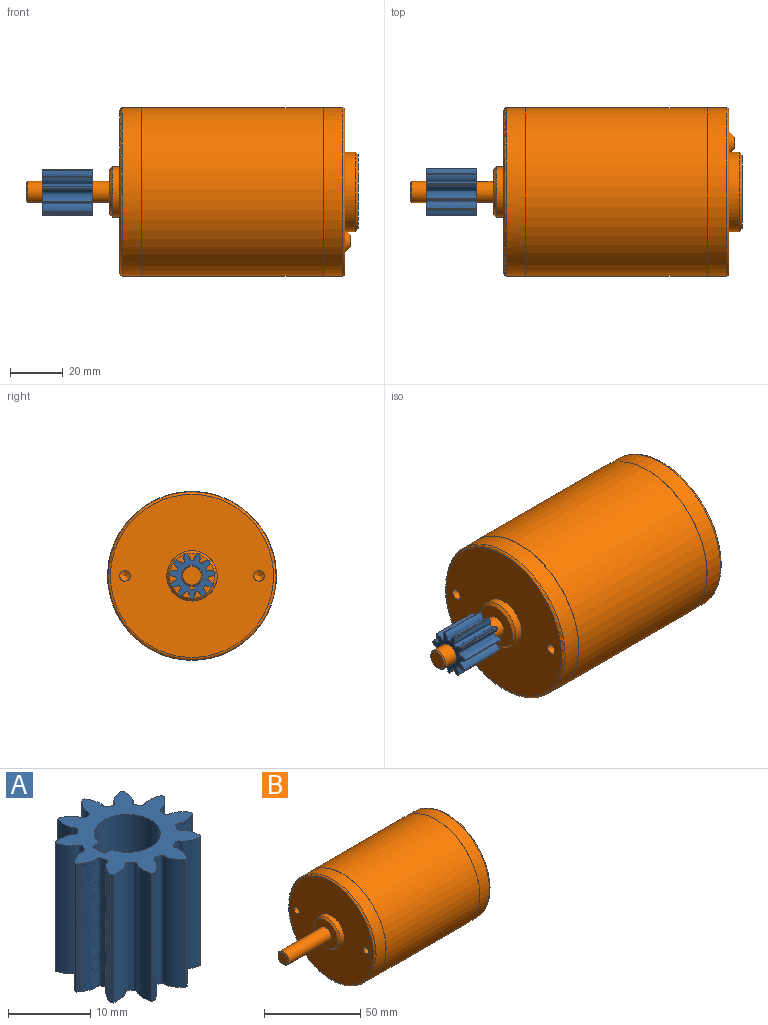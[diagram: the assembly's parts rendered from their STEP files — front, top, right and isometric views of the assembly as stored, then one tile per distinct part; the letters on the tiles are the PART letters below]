
ASSEMBLY  parts=2 mates=1
PART A: 34 faces, bbox 17.6x17.7x19.1 mm
  f0: cylinder r=4mm len=19.05mm, axis (0,0,1), area 439.9mm2, adj f17,f19,f31,f32
  f1: bspline ~9.53x0.35mm, area 4.2mm2, adj f6,f11,f17,f25
  f2: bspline ~9.53x0.41mm, area 4.2mm2, adj f3,f16,f17,f21
  f3: bspline ~9.53x0.41mm, area 4.2mm2, adj f2,f16,f19,f21
  f4: bspline ~19.05x0.44mm, area 8.3mm2, adj f15,f17,f19,f21
  f5: bspline ~19.05x0.41mm, area 8.3mm2, adj f12,f17,f19,f25
  f6: bspline ~9.53x0.35mm, area 4.2mm2, adj f1,f11,f19,f25
  f7: cylinder r=8.94mm len=19.05mm, axis (0,0,1), area 7.5mm2, adj f17,f19,f29,f30
  f8: cylinder r=8.94mm len=19.05mm, axis (0,0,1), area 7.5mm2, adj f17,f19,f28,f29
  f9: cylinder r=8.94mm len=19.05mm, axis (0,0,1), area 7.5mm2, adj f17,f19,f27,f28
  f10: cylinder r=8.94mm len=19.05mm, axis (0,0,1), area 7.5mm2, adj f17,f19,f26,f27
  f11: cylinder r=8.94mm len=19.05mm, axis (0,0,1), area 7.5mm2, adj f1,f6,f17,f19,f26
  f12: cylinder r=8.94mm len=19.05mm, axis (0,0,1), area 7.5mm2, adj f5,f17,f19,f24
  f13: cylinder r=8.94mm len=19.05mm, axis (0,0,1), area 7.5mm2, adj f17,f19,f23,f24
  f14: cylinder r=8.94mm len=19.05mm, axis (0,0,1), area 7.5mm2, adj f17,f19,f22,f23
  f15: cylinder r=8.94mm len=19.05mm, axis (0,0,1), area 7.5mm2, adj f4,f17,f19,f22
  f16: cylinder r=8.94mm len=19.05mm, axis (0,0,1), area 7.5mm2, adj f2,f3,f17,f19,f20
  f17: plane 17.74x17.57mm, normal (0,0,1), area 121.8mm2, adj f0,f1,f2,f4,f5,f7,f8,f9
  f18: cylinder r=8.94mm len=19.05mm, axis (0,0,1), area 7.5mm2, adj f17,f19,f20,f30
  f19: plane 17.74x17.57mm, normal (0,0,-1), area 121.8mm2, adj f0,f3,f4,f5,f6,f7,f8,f9
  f20: bspline ~19.05x4.65mm, area 140.4mm2, adj f16,f17,f18,f19
  f21: bspline ~19.05x3.33mm, area 123.7mm2, adj f2,f3,f4,f17,f19
  f22: bspline ~19.05x4.23mm, area 140.4mm2, adj f14,f15,f17,f19
  f23: bspline ~19.05x4.61mm, area 140.4mm2, adj f13,f14,f17,f19
  f24: bspline ~19.05x3.78mm, area 140.4mm2, adj f12,f13,f17,f19
  f25: bspline ~19.05x3.79mm, area 123.7mm2, adj f1,f5,f6,f17,f19
  f26: bspline ~19.05x4.47mm, area 140.4mm2, adj f10,f11,f17,f19
  f27: bspline ~19.05x3.78mm, area 140.4mm2, adj f9,f10,f17,f19
  f28: bspline ~19.05x4.61mm, area 140.4mm2, adj f8,f9,f17,f19
  f29: bspline ~19.05x4.23mm, area 140.4mm2, adj f7,f8,f17,f19
  f30: bspline ~19.05x3.92mm, area 140.4mm2, adj f7,f17,f18,f19
  f31: plane 19.05x1.13mm, normal (0,-1,0), area 21.5mm2, adj f0,f17,f19,f33
  f32: plane 19.05x1.13mm, normal (0,1,0), area 21.5mm2, adj f0,f17,f19,f33
  f33: plane 19.05x2.02mm, normal (1,0,0), area 38.5mm2, adj f17,f19,f31,f32
PART B: 33 faces, bbox 125.8x69x69 mm
  f0: cone r=4mm half-angle=45deg, axis (1,0,0), area 16.7mm2, adj f18,f22
  f1: cone r=9.53mm half-angle=45deg, axis (1,0,0), area 81.4mm2, adj f13,f27
  f2: cone r=14.02mm half-angle=45deg, axis (-1,0,0), area 131.2mm2, adj f17,f23
  f3: cone r=2.12mm half-angle=45deg, axis (-1,0,0), area 62.9mm2, adj f5,f29
  f4: cone r=2.12mm half-angle=45deg, axis (-1,0,0), area 62.9mm2, adj f6,f28
  f5: cylinder r=4.32mm len=8.64mm, axis (-1,0,0), area 1.3mm2, adj f3,f21
  f6: cylinder r=4.32mm len=8.64mm, axis (-1,0,0), area 1.3mm2, adj f4,f21
  f7: cone r=2.02mm half-angle=59deg, axis (-1,0,0), area 14.9mm2, adj f8
  f8: cylinder r=2.02mm len=13.61mm, axis (-1,0,0), area 172.7mm2, adj f7,f26
  f9: cone r=2.02mm half-angle=59deg, axis (-1,0,0), area 14.9mm2, adj f10
  f10: cylinder r=2.02mm len=13.61mm, axis (-1,0,0), area 172.7mm2, adj f9,f26
  f11: torus R=30.88mm, axis (1,0,0), area 311mm2, adj f16,f21
  f12: torus R=30.88mm, axis (-1,0,0), area 311mm2, adj f14,f26
  f13: cylinder r=9.53mm len=19.05mm, axis (1,0,0), area 178.6mm2, adj f1,f26
  f14: cylinder r=31.88mm len=63.75mm, axis (1,0,0), area 1448mm2, adj f12,f25
  f15: cylinder r=32mm len=68.76mm, axis (1,0,0), area 13826.1mm2, adj f24,f25
  f16: cylinder r=31.88mm len=63.75mm, axis (1,0,0), area 1448mm2, adj f11,f24
  f17: cylinder r=15.04mm len=30.07mm, axis (1,0,0), area 376.4mm2, adj f2,f21
  f18: cylinder r=4mm len=31.1mm, axis (1,0,0), area 739mm2, adj f0,f19,f20,f27,f31,f32
  f19: cylinder r=1mm len=2mm, axis (0,1,0), area 3.4mm2, adj f18,f30,f31,f32
  f20: cylinder r=1mm len=2mm, axis (0,-1,0), area 3.4mm2, adj f18,f30,f31,f32
  f21: plane 61.75x61.75mm, normal (1,0,0), area 2167.7mm2, adj f5,f6,f11,f17
  f22: plane 7x7mm, normal (-1,0,0), area 38.5mm2, adj f0
  f23: plane 28.04x28.04mm, normal (1,0,0), area 617.6mm2, adj f2
  f24: plane 64.01x64.01mm, normal (1,0,0), area 25.5mm2, adj f15,f16
  f25: plane 64.01x64.01mm, normal (-1,0,0), area 25.5mm2, adj f14,f15
  f26: plane 61.75x61.75mm, normal (-1,0,0), area 2684.5mm2, adj f8,f10,f12,f13
  f27: plane 17.02x17.02mm, normal (-1,0,0), area 177.2mm2, adj f1,f18
  f28: plane 4.24x4.24mm, normal (1,0,0), area 14.1mm2, adj f4
  f29: plane 4.24x4.24mm, normal (1,0,0), area 14.1mm2, adj f3
  f30: plane 21.5x2mm, normal (0,1,0), area 42.1mm2, adj f19,f20,f31,f32
  f31: plane 19.5x1.07mm, normal (0,0,1), area 20.9mm2, adj f18,f19,f20,f30
  f32: plane 19.5x1.07mm, normal (0,0,-1), area 20.9mm2, adj f18,f19,f20,f30
PLACE A rot(axis=(0,-1,0),90deg) t=(-68.49,-38.92,7.43)mm
PLACE B t=(-48.61,-38.92,7.51)mm
MATE fastened A.f19 <-> B.f0  axis (1,0,0) through (-58.96,-38.92,7.51)mm
